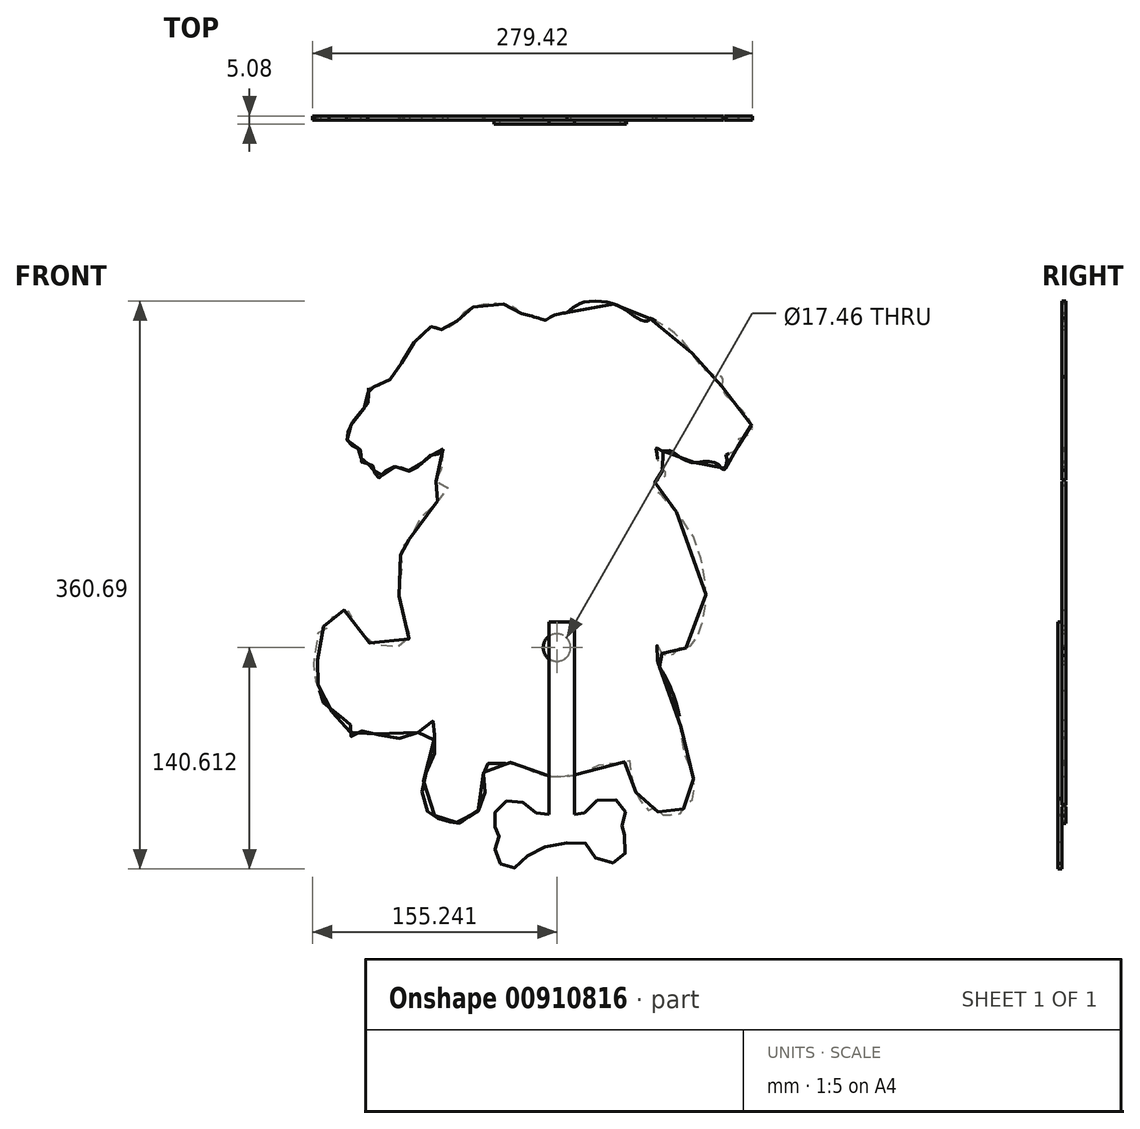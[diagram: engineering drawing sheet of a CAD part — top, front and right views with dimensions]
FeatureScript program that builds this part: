
annotation { "Feature Type Name" : "Feature", "Feature Type Description" : "" }
export const myFeature = defineFeature(function(context is Context, id is Id, definition is map)
    precondition{}
    {
        {
            var Q0;
            Q0=qCreatedBy(makeId("Front.planeOp"),FACE);
            var sketch = newSketch(context, id + "F0", { "sketchPlane" : qUnion([Q0])});
            skFitSpline(sketch, "E0", {"points": [v(382.8, 398.37) * mm, v(373.43, 404.25) * mm, v(349.49, 401.42) * mm, v(341.43, 393.36) * mm, v(333.16, 388.36) * mm, v(329.02, 389.23) * mm, v(326.85, 390.5) * mm, v(318.83, 385.06) * mm, v(308.21, 370.56) * mm, v(303.1, 360.93) * mm, v(293.85, 353.2) * mm, v(287.54, 351.77) * mm, v(285.2, 350.93) * mm, v(285.14, 349.06) * mm, v(285.3, 342.2) * mm, v(278.3, 333.66) * mm, v(272.74, 323.82) * mm, v(271.7, 318.51) * mm, v(274.03, 315.4) * mm, v(279.81, 312.33) * mm, v(280.73, 310.13) * mm, v(280.66, 306.35) * mm, v(281.31, 303.84) * mm, v(284.58, 303.3) * mm, v(287.74, 302.32) * mm, v(289.04, 299.6) * mm, v(291.21, 293.83) * mm, v(294.91, 296.87) * mm, v(300.57, 300.9) * mm, v(305.69, 300.68) * mm, v(310.91, 298.4) * mm, v(316.9, 301.01) * mm, v(322.02, 306.13) * mm, v(324.95, 308.41) * mm, v(330.07, 309.4) * mm, v(332.9, 312.33) * mm], "startDerivative": vector(-191.44, 190.13) * mm, "endDerivative": vector(99.62, 154.71) * mm});
            skFitSpline(sketch, "E1", {"points": [v(332.9, 312.33) * mm, v(332.9, 305.26) * mm, v(331.05, 298.4) * mm, v(327.02, 296.44) * mm, v(327.08, 294.14) * mm, v(331.54, 289.37) * mm, v(335.4, 289.37) * mm, v(335.85, 287.06) * mm, v(335.4, 282.44) * mm, v(330.07, 279.93) * mm, v(322.02, 272.24) * mm, v(314.5, 263.27) * mm, v(312.68, 257.23) * mm, v(308.47, 252.65) * mm, v(306.02, 252.1) * mm, v(306.87, 250.03) * mm, v(308.25, 248.33) * mm, v(308.25, 246.8) * mm, v(306.63, 246.02) * mm, v(305.87, 245.18) * mm, v(306.56, 244.87) * mm, v(307.48, 243.48) * mm, v(307.17, 241.1) * mm, v(305.1, 228.21) * mm, v(305.03, 218.2) * mm, v(307.34, 207.26) * mm, v(310.2, 197.57) * mm, v(311.83, 193.62) * mm, v(309.75, 189.85) * mm, v(305.82, 186.93) * mm, v(299.36, 186.7) * mm, v(288.74, 188.31) * mm, v(281.8, 192.47) * mm, v(277.88, 200.94) * mm, v(275.19, 207.7) * mm, v(269.03, 210.1) * mm, v(263.87, 207.25) * mm, v(260.49, 201.63) * mm, v(260.26, 197.7) * mm, v(259.16, 198.1) * mm, v(256.9, 199.87) * mm, v(256.2, 200.33) * mm, v(253.77, 196.58) * mm, v(251.49, 187.65) * mm, v(251.6, 182) * mm, v(253.47, 176.32) * mm, v(252.1, 175.61) * mm, v(250.15, 175.67) * mm, v(249.98, 174.36) * mm, v(251.29, 166.46) * mm, v(253.3, 162.7) * mm, v(254.91, 159.92) * mm, v(255.3, 159.02) * mm, v(252.84, 158.82) * mm, v(253.17, 156.88) * mm, v(259.32, 148.53) * mm, v(269.08, 141.47) * mm, v(273.1, 140.56) * mm, v(273.87, 139.07) * mm, v(274.06, 136.94) * mm, v(273.9, 134.02) * mm, v(274.13, 131.8) * mm, v(274.7, 129.67) * mm, v(276.56, 130.75) * mm, v(280.02, 133.06) * mm, v(283.1, 133.29) * mm, v(288.41, 131.9) * mm, v(297.72, 129.6) * mm, v(305.5, 128.67) * mm, v(312.27, 130.51) * mm, v(319.05, 133.44) * mm, v(324.95, 138.14) * mm, v(327.44, 140.3) * mm, v(327.82, 137.6) * mm, v(327.29, 126.04) * mm, v(327.67, 120.08) * mm, v(326, 116.72) * mm, v(322.02, 106.85) * mm, v(319.77, 98.95) * mm, v(319.77, 92.35) * mm, v(322.02, 84.32) * mm, v(324.95, 80.18) * mm, v(328.83, 79.53) * mm, v(330.07, 77.07) * mm, v(332.9, 75.26) * mm, v(336.98, 75.4) * mm, v(338.54, 76.56) * mm, v(339.96, 75.78) * mm, v(342.3, 74.87) * mm, v(345.66, 75) * mm, v(348.25, 76.82) * mm, v(348.9, 78.76) * mm, v(350.06, 80.18) * mm, v(353.55, 80.57) * mm, v(356.66, 86.27) * mm, v(359, 92.22) * mm, v(359.38, 99.21) * mm, v(358.34, 105.68) * mm, v(359.38, 109.44) * mm, v(360.29, 112.54) * mm, v(362.62, 112.67) * mm, v(369.22, 111.9) * mm, v(374.83, 113.42) * mm, v(381.78, 111.68) * mm, v(388.83, 108.02) * mm, v(394.6, 105.92) * mm, v(400.64, 104.63) * mm, v(416.43, 105.42) * mm, v(427.75, 109.88) * mm, v(436.14, 113.04) * mm, v(446.81, 113.38) * mm, v(451.43, 114.7) * mm, v(452.2, 110) * mm, v(452.74, 101.84) * mm, v(454.13, 97.07) * mm, v(457.28, 90.22) * mm, v(461.75, 83.52) * mm, v(465.15, 83.41) * mm, v(466.18, 85.32) * mm, v(467.87, 83.63) * mm, v(471.46, 80.58) * mm, v(475.05, 80.1) * mm, v(476.69, 80.64) * mm, v(477.68, 79.67) * mm, v(481.76, 80.06) * mm, v(485.15, 82.68) * mm, v(486.61, 86.52) * mm, v(488.84, 86.37) * mm, v(490.85, 88.99) * mm, v(492.54, 94.14) * mm, v(492, 102.23) * mm, v(489.08, 112.7) * mm, v(485.01, 122.83) * mm, v(484.14, 133.82) * mm, v(481.42, 149.06) * mm, v(474.16, 167.5) * mm, v(469.63, 175.4) * mm, v(469, 180.2) * mm, v(468.69, 187.59) * mm, v(468.98, 187.3) * mm, v(470.53, 186.93) * mm, v(471.02, 184.02) * mm, v(472.54, 181.98) * mm, v(477.04, 181.34) * mm, v(480.2, 182.99) * mm, v(483.23, 186.47) * mm, v(484, 186.97) * mm, v(484.38, 186.27) * mm, v(486.87, 185.94) * mm, v(492.04, 189.43) * mm, v(496.5, 198.57) * mm, v(499.72, 220.44) * mm, v(492.28, 255.68) * mm, v(479.35, 274.3) * mm, v(470.88, 283.85) * mm, v(467.69, 286) * mm, v(466.07, 287.23) * mm, v(466.59, 289.43) * mm, v(467.43, 291.72) * mm, v(467.8, 292.73) * mm, v(469.72, 292.64) * mm, v(471.45, 293.57) * mm, v(474.05, 295.53) * mm, v(474.88, 297) * mm, v(474.42, 297.78) * mm, v(473.14, 298.05) * mm, v(470.94, 300.84) * mm, v(468.93, 306.13) * mm, v(468.39, 311.73) * mm, v(468.2, 313.38) * mm, v(469.9, 312.33) * mm, v(472.6, 311.22) * mm, v(476.72, 311.6) * mm, v(479, 310.54) * mm, v(482.3, 307.84) * mm, v(487.88, 304.73) * mm, v(493.06, 303.76) * mm, v(499.9, 304.68) * mm, v(505.77, 303.7) * mm, v(508.87, 301.64) * mm, v(510.83, 299.13) * mm, v(512.14, 300.38) * mm, v(512.52, 301.9) * mm, v(513.34, 304.47) * mm, v(512.47, 308.41) * mm, v(514.15, 309.4) * mm, v(518.04, 311.34) * mm, v(520.18, 314.38) * mm, v(520.63, 317.3) * mm, v(520.44, 318.98) * mm, v(522.32, 319.5) * mm, v(526.18, 321.46) * mm, v(529.26, 324.77) * mm, v(527.72, 330.16) * mm, v(523.8, 335.86) * mm, v(514.13, 344.9) * mm, v(510, 351.76) * mm, v(510.78, 358.37) * mm, v(508.43, 358.16) * mm, v(499.52, 362.66) * mm, v(487.07, 378.5) * mm, v(476.14, 388.97) * mm, v(465.67, 395.07) * mm, v(464.26, 395.4) * mm, v(463.93, 394.3) * mm, v(460.34, 393.87) * mm, v(454.9, 396.49) * mm, v(446.73, 402.04) * mm, v(436.7, 405.8) * mm, v(423.1, 405.8) * mm, v(416.45, 402.86) * mm, v(411.55, 399.05) * mm], "startDerivative": vector(23.33, -1189.18) * mm, "endDerivative": vector(-898.46, -745.48) * mm});
            skFitSpline(sketch, "E2", {"points": [v(411.55, 399.05) * mm, v(406.63, 398.29) * mm, v(401.08, 396.17) * mm, v(398.09, 394.37) * mm, v(393.84, 395.4) * mm, v(387.36, 397.25) * mm, v(382.8, 398.37) * mm], "startDerivative": vector(-28.51, -3.16) * mm, "endDerivative": vector(-26.63, 6.41) * mm});
            skSolve(sketch);
        }
        {
            var Q0;
            Q0 = qSketchRegion(id + "F0", true);
            extrude(context, id + "F1", {"entities" : qUnion([Q0]), "depth" : 2.54 * mm, "offsetDistance" : 25.4 * mm});
        }
        {
            var Q0;
            Q0=makeQuery(id+"F1.opExtrude","CAP_FACE",FACE,{"disambiguationData":[OSD([sQuery(id+"F0.wireOp",EDGE,"E0"),sQuery(id+"F0.wireOp",EDGE,"E1"),sQuery(id+"F0.wireOp",EDGE,"E2")])],"isStart":false});
            var sketch = newSketch(context, id + "F2", { "sketchPlane" : qUnion([Q0])});
            skFitSpline(sketch, "E3", {"points": [v(400.17, 80.27) * mm, v(395.63, 80.35) * mm, v(389.78, 82.66) * mm, v(383.16, 88.2) * mm, v(375, 89.43) * mm, v(367.46, 84.97) * mm, v(365.3, 78.2) * mm, v(365.92, 72.5) * mm, v(368.84, 68.2) * mm, v(368.54, 66.34) * mm, v(366.23, 61.26) * mm, v(366.23, 55.88) * mm, v(369.46, 48.95) * mm, v(375.15, 45.72) * mm, v(382.7, 49.26) * mm, v(389.16, 56.65) * mm, v(403.02, 60.65) * mm, v(415.95, 62.8) * mm, v(424.72, 61.1) * mm, v(429.5, 52.95) * mm, v(439.04, 49.26) * mm, v(446.43, 52.18) * mm, v(449.2, 60.19) * mm, v(447.2, 69.27) * mm, v(445.66, 70.8) * mm, v(447.2, 74.04) * mm, v(448.59, 79.9) * mm, v(446.74, 87.28) * mm, v(437.96, 90.36) * mm, v(428.27, 87.74) * mm, v(422.26, 81.12) * mm, v(418.3, 79.77) * mm, v(416.2, 80.2) * mm], "startDerivative": vector(-181.82, -13) * mm, "endDerivative": vector(-126.6, 57.4) * mm});
            skLineSegment(sketch, "E4", {"start": v(416.2, 80.2) * mm, "end": v(416.2, 202.52) * mm});
            skLineSegment(sketch, "E5", {"start": v(416.2, 202.52) * mm, "end": v(400.17, 202.52) * mm});
            skLineSegment(sketch, "E6", {"start": v(400.17, 80.27) * mm, "end": v(400.17, 202.52) * mm});
            skSolve(sketch);
        }
        {
            var Q0;
            Q0 = qSketchRegion(id + "F2", true);
            extrude(context, id + "F3", {"entities" : qUnion([Q0]), "depth" : 2.54 * mm, "offsetDistance" : 25.4 * mm});
        }
        {
            var Q0;
            Q0=makeQuery(id+"F1.opExtrude","CAP_FACE",FACE,{"disambiguationData":[OSD([sQuery(id+"F0.wireOp",EDGE,"E0"),sQuery(id+"F0.wireOp",EDGE,"E1"),sQuery(id+"F0.wireOp",EDGE,"E2")])],"isStart":false});
            var sketch = newSketch(context, id + "F4", { "sketchPlane" : qUnion([Q0])});
            skCircle(sketch, "E7", {"center": v(405.16, 186.32) * mm, "radius": 50.8 * mm, "construction": true});
            skCircle(sketch, "E8", {"center": v(405.16, 186.32) * mm, "radius": 8.73 * mm});
            skSolve(sketch);
        }
        {
            var Q0;
            Q0 = qSketchRegion(id + "F4", true);
            extrude(context, id + "F5", {"entities" : qUnion([Q0]), "operationType" : NewBodyOperationType.REMOVE, "endBound" : BoundingType.THROUGH_ALL, "oppositeDirection" : true, "depth" : 25.4 * mm, "offsetDistance" : 25.4 * mm});
        }
    });
